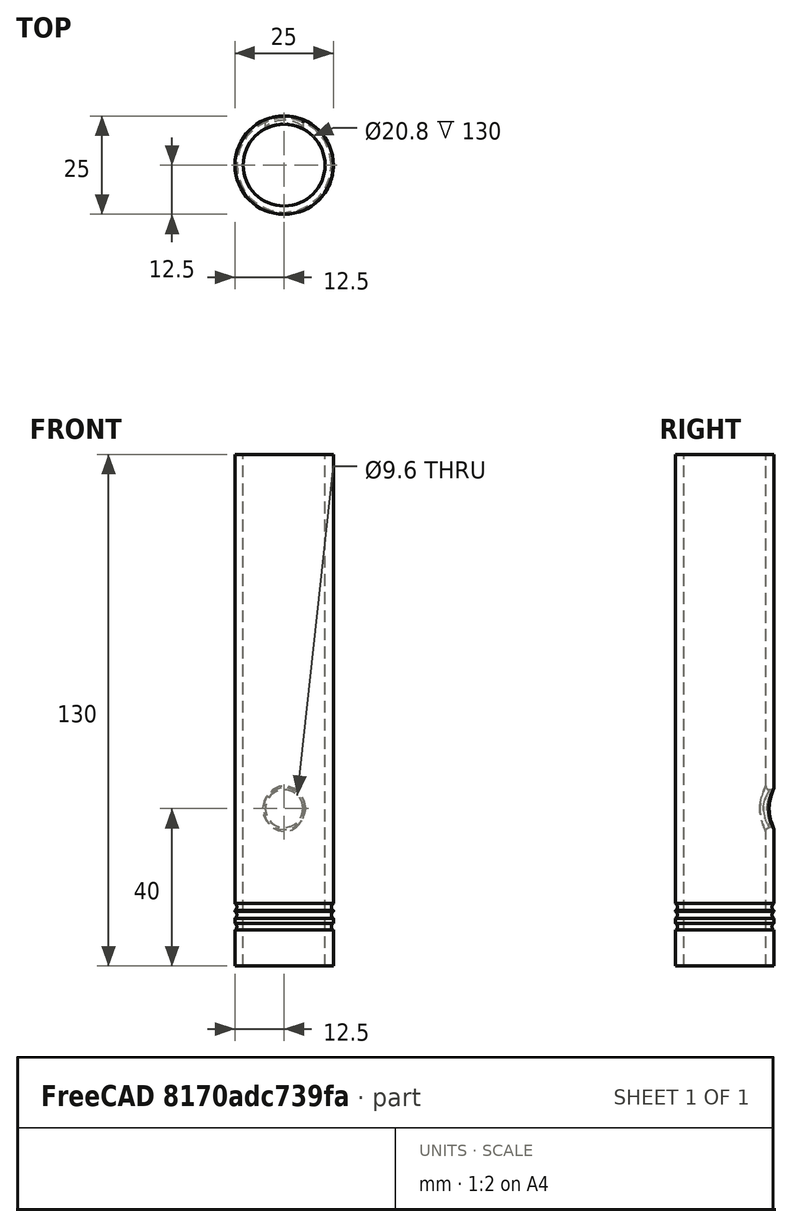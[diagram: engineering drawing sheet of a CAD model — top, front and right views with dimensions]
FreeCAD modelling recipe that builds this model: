
FCSTD DOCUMENT
Label: Part3
License: CC-BY 3.0
LicenseURL: http://creativecommons.org/licenses/by/3.0/
objects: Part::Cut×5, Part::Cylinder×3, Part::Torus×3, PartDesign::Fillet×2
note: 13 computed .brp shape members not serialized (recipe doc carries the construction recipe); baked Part::Feature solids carry a one-line shape summary decoded from their .brp

FEATURE [Part::Cylinder] Cylinder001
  Angle = 360
  Height = 130
  Radius = 10.4
FEATURE [Part::Cylinder] Cylinder
  Angle = 360
  Height = 130
  Radius = 12.5
FEATURE [Part::Cut] Cut
  Base = -> Cylinder
  Tool = -> Cylinder001
FEATURE [Part::Torus] Torus001
  Angle1 = -180
  Angle2 = 180
  Angle3 = 360
  Placement = pos=(0,0,10) rot=(0,0,1;0rad)
  Radius1 = 13
  Radius2 = 1
FEATURE [Part::Torus] Torus
  Angle1 = -180
  Angle2 = 180
  Angle3 = 360
  Placement = pos=(0,0,13) rot=(0,0,1;0rad)
  Radius1 = 13
  Radius2 = 1
FEATURE [Part::Cylinder] Cylinder004  label="Asiran"
  Angle = 360
  Height = 10
  Placement = pos=(0,15,40) rot=(1,0,0;1.5708rad)
  Radius = 4.8
FEATURE [Part::Cut] Cut001
  Base = -> Cut
  Tool = -> Cylinder004
FEATURE [Part::Cut] Cut002
  Base = -> Cut001
  Tool = -> Torus001
FEATURE [Part::Torus] Torus002
  Angle1 = -180
  Angle2 = 180
  Angle3 = 360
  Placement = pos=(0,0,15) rot=(0,0,1;0rad)
  Radius1 = 13
  Radius2 = 1
FEATURE [Part::Cut] Cut003
  Base = -> Cut002
  Tool = -> Torus
FEATURE [Part::Cut] Cut004
  Base = -> Cut003
  Tool = -> Torus002
FEATURE [PartDesign::Fillet] Fillet
  Base = -> Cut004 [Edge14]
  Radius = 0.5
FEATURE [PartDesign::Fillet] Fillet001
  Base = -> Fillet [Edge3]
  Radius = 1
